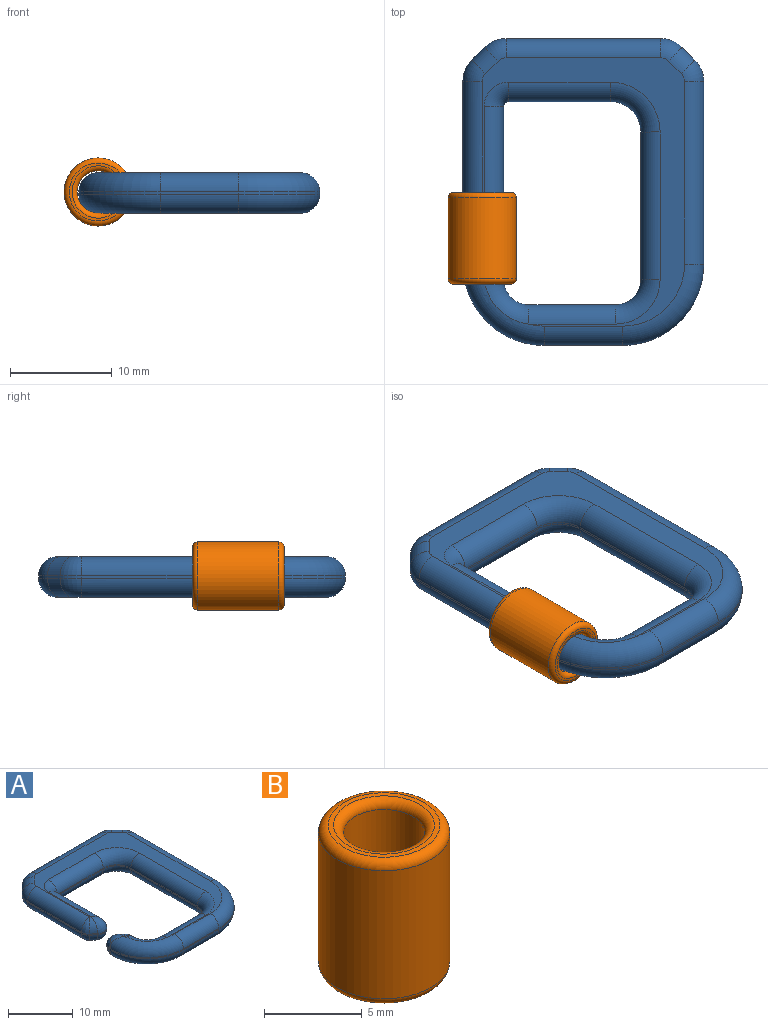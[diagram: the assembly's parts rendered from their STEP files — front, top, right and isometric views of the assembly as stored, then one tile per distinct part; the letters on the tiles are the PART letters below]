
ASSEMBLY  parts=2 mates=1
PART A: 90 faces, bbox 25x30.9x4.6 mm
  f0: plane 0.54x0.12mm, normal (0,0,-1), area 0mm2, adj f63,f66,f67,f70,f74
  f1: plane 0.54x0.12mm, normal (0,0,1), area 0mm2, adj f32,f36,f37,f42,f44
  f2: plane 15.21x0.2mm, normal (0,1,0), area 3mm2, adj f28,f31,f58,f88
  f3: plane 1.24x1.24mm, normal (-0.71,0.71,0), area 0.4mm2, adj f28,f29,f59,f87
  f4: plane 11.76x0.2mm, normal (-1,0,0), area 2.4mm2, adj f5,f29,f55,f83
  f5: cylinder r=1.5mm len=1.15mm, axis (0,0,-1), area 0.3mm2, adj f4,f6,f53,f81
  f6: plane 1x0.84mm, normal (-0.65,-0.76,0), area 0.3mm2, adj f5,f7,f51,f79
  f7: cylinder r=1.5mm len=2.47mm, axis (0,0,-1), area 0.7mm2, adj f6,f8,f49,f77
  f8: plane 10.14x0.2mm, normal (1,0,0), area 2mm2, adj f7,f9,f47,f75
  f9: cylinder r=0.5mm len=0.5mm, axis (0,0,-1), area 0.2mm2, adj f8,f10,f45,f73
  f10: plane 10x0.2mm, normal (0,-1,0), area 2mm2, adj f9,f11,f43,f69
  f11: cylinder r=3mm len=3mm, axis (0,0,-1), area 0.9mm2, adj f10,f12,f39,f64
  f12: plane 14.5x0.2mm, normal (-1,0,0), area 2.9mm2, adj f11,f13,f34,f61
  f13: cylinder r=2.5mm len=2.5mm, axis (0,0,-1), area 0.8mm2, adj f12,f14,f33,f62
  f14: plane 8.5x0.2mm, normal (0,1,0), area 1.7mm2, adj f13,f15,f38,f65
  f15: cylinder r=2.5mm len=2.5mm, axis (0,0,-1), area 0.8mm2, adj f14,f16,f42,f70
  f16: plane 0.34x0.2mm, normal (1,0,0), area 0.1mm2, adj f15,f17,f37,f66
  f17: cylinder r=2mm len=1.53mm, axis (0,0,-1), area 0.3mm2, adj f16,f18,f32,f63
  f18: plane 0.99x0.83mm, normal (0.65,0.76,0), area 0.3mm2, adj f17,f19,f36,f67
  f19: cylinder r=1.4mm len=2.3mm, axis (0,0,-1), area 0.6mm2, adj f18,f20,f35,f68
  f20: plane 0.2x0.13mm, normal (-1,0,0), area 0mm2, adj f19,f21,f40,f72
  f21: cylinder r=8mm len=8mm, axis (0,0,-1), area 2.5mm2, adj f20,f22,f44,f74
  f22: plane 7.7x0.2mm, normal (0,-1,0), area 1.5mm2, adj f21,f23,f46,f76
  f23: cylinder r=8mm len=8mm, axis (0,0,-1), area 2.5mm2, adj f22,f24,f48,f78
  f24: plane 17.96x0.2mm, normal (1,0,0), area 3.6mm2, adj f23,f30,f50,f80
  f25: plane 1.24x1.24mm, normal (0.71,0.71,0), area 0.4mm2, adj f30,f31,f54,f84
  f26: plane 26.4x19.9mm, normal (0,0,1), area 109.1mm2, adj f33,f34,f38,f39,f42,f43,f44,f45
  f27: plane 26.4x19.9mm, normal (0,0,-1), area 109.1mm2, adj f61,f62,f64,f65,f69,f70,f73,f74
  f28: cylinder r=3mm len=2.12mm, axis (0,0,-1), area 0.5mm2, adj f2,f3,f60,f89
  f29: cylinder r=3mm len=2.12mm, axis (0,0,1), area 0.5mm2, adj f3,f4,f57,f85
  f30: cylinder r=3mm len=2.12mm, axis (0,0,-1), area 0.5mm2, adj f24,f25,f52,f82
  f31: cylinder r=3mm len=2.12mm, axis (0,0,-1), area 0.5mm2, adj f2,f25,f56,f86
  f32: torus R=0.1mm, axis (0,0,1), area 3.4mm2, adj f1,f17,f36,f37
  f33: torus R=4.4mm, axis (0,0,1), area 15mm2, adj f13,f26,f34,f38
  f34: cylinder r=1.9mm len=14.5mm, axis (0,1,0), area 43.3mm2, adj f12,f26,f33,f39
  f35: bspline ~3.22x2.38mm, area 4mm2, adj f19,f36,f40,f41
  f36: cylinder r=1.9mm len=2.29mm, axis (0.76,-0.65,0), area 2.6mm2, adj f1,f18,f32,f35,f41
  f37: cylinder r=1.9mm len=1.9mm, axis (0,-1,0), area 1mm2, adj f1,f16,f32,f42
  f38: cylinder r=1.9mm len=8.5mm, axis (1,0,0), area 25.4mm2, adj f14,f26,f33,f42
  f39: torus R=4.9mm, axis (0,0,1), area 17.3mm2, adj f11,f26,f34,f43
  f40: cylinder r=1.9mm len=0.92mm, axis (0,1,0), area 0.1mm2, adj f20,f35,f44
  f41: bspline ~2.71x2.13mm, area 2mm2, adj f35,f36,f44
  f42: torus R=4.4mm, axis (0,0,1), area 14mm2, adj f1,f15,f26,f37,f38,f44
  f43: cylinder r=1.9mm len=10mm, axis (-1,0,0), area 29.8mm2, adj f10,f26,f39,f45
  f44: torus R=6.1mm, axis (0,0,1), area 32.2mm2, adj f1,f21,f26,f40,f41,f42,f46
  f45: torus R=2.4mm, axis (0,0,1), area 5.6mm2, adj f9,f26,f43,f47
  f46: cylinder r=1.9mm len=7.7mm, axis (-1,0,0), area 23mm2, adj f22,f26,f44,f48
  f47: cylinder r=1.9mm len=10.14mm, axis (0,-1,0), area 29mm2, adj f8,f26,f45,f49
  f48: torus R=6.1mm, axis (0,0,1), area 34.3mm2, adj f23,f26,f46,f50
  f49: bspline ~4.09x3.28mm, area 7mm2, adj f7,f47,f51
  f50: cylinder r=1.9mm len=17.96mm, axis (0,-1,0), area 53.6mm2, adj f24,f26,f48,f52
  f51: cylinder r=1.9mm len=2.3mm, axis (-0.76,0.65,0), area 2.7mm2, adj f6,f26,f49,f53
  f52: torus R=1.1mm, axis (0,0,1), area 5.4mm2, adj f26,f30,f50,f54
  f53: bspline ~2.19x1.9mm, area 2.5mm2, adj f5,f51,f55
  f54: cylinder r=1.9mm len=2.59mm, axis (0.71,-0.71,0), area 5.2mm2, adj f25,f26,f52,f56
  f55: cylinder r=1.9mm len=11.76mm, axis (0,1,0), area 34.8mm2, adj f4,f26,f53,f57
  f56: torus R=1.1mm, axis (0,0,1), area 5.4mm2, adj f26,f31,f54,f58
  f57: torus R=1.1mm, axis (0,0,1), area 5.4mm2, adj f26,f29,f55,f59
  f58: cylinder r=1.9mm len=15.21mm, axis (1,0,0), area 45.4mm2, adj f2,f26,f56,f60
  f59: cylinder r=1.9mm len=2.59mm, axis (0.71,0.71,0), area 5.2mm2, adj f3,f26,f57,f60
  f60: torus R=1.1mm, axis (0,0,1), area 5.4mm2, adj f26,f28,f58,f59
  f61: cylinder r=1.9mm len=14.5mm, axis (0,-1,0), area 43.3mm2, adj f12,f27,f62,f64
  f62: torus R=4.4mm, axis (0,0,1), area 15mm2, adj f13,f27,f61,f65
  f63: torus R=0.1mm, axis (0,0,1), area 3.4mm2, adj f0,f17,f66,f67
  f64: torus R=4.9mm, axis (0,0,1), area 17.3mm2, adj f11,f27,f61,f69
  f65: cylinder r=1.9mm len=8.5mm, axis (-1,0,0), area 25.4mm2, adj f14,f27,f62,f70
  f66: cylinder r=1.9mm len=1.9mm, axis (0,1,0), area 1mm2, adj f0,f16,f63,f70
  f67: cylinder r=1.9mm len=2.29mm, axis (-0.76,0.65,0), area 2.6mm2, adj f0,f18,f63,f68,f71
  f68: bspline ~3.22x2.38mm, area 4mm2, adj f19,f67,f71,f72
  f69: cylinder r=1.9mm len=10mm, axis (1,0,0), area 29.8mm2, adj f10,f27,f64,f73
  f70: torus R=4.4mm, axis (0,0,1), area 14mm2, adj f0,f15,f27,f65,f66,f74
  f71: bspline ~2.71x2.13mm, area 2mm2, adj f67,f68,f74
  f72: cylinder r=1.9mm len=0.92mm, axis (0,-1,0), area 0.1mm2, adj f20,f68,f74
  f73: torus R=2.4mm, axis (0,0,1), area 5.6mm2, adj f9,f27,f69,f75
  f74: torus R=6.1mm, axis (0,0,1), area 32.2mm2, adj f0,f21,f27,f70,f71,f72,f76
  f75: cylinder r=1.9mm len=10.14mm, axis (0,1,0), area 29mm2, adj f8,f27,f73,f77
  f76: cylinder r=1.9mm len=7.7mm, axis (1,0,0), area 23mm2, adj f22,f27,f74,f78
  f77: bspline ~4.09x3.28mm, area 7mm2, adj f7,f75,f79
  f78: torus R=6.1mm, axis (0,0,1), area 34.3mm2, adj f23,f27,f76,f80
  f79: cylinder r=1.9mm len=2.3mm, axis (0.76,-0.65,0), area 2.7mm2, adj f6,f27,f77,f81
  f80: cylinder r=1.9mm len=17.96mm, axis (0,1,0), area 53.6mm2, adj f24,f27,f78,f82
  f81: bspline ~2.19x1.9mm, area 2.5mm2, adj f5,f79,f83
  f82: torus R=1.1mm, axis (0,0,1), area 5.4mm2, adj f27,f30,f80,f84
  f83: cylinder r=1.9mm len=11.76mm, axis (0,-1,0), area 34.8mm2, adj f4,f27,f81,f85
  f84: cylinder r=1.9mm len=2.59mm, axis (-0.71,0.71,0), area 5.2mm2, adj f25,f27,f82,f86
  f85: torus R=1.1mm, axis (0,0,1), area 5.4mm2, adj f27,f29,f83,f87
  f86: torus R=1.1mm, axis (0,0,1), area 5.4mm2, adj f27,f31,f84,f88
  f87: cylinder r=1.9mm len=2.59mm, axis (-0.71,-0.71,0), area 5.2mm2, adj f3,f27,f85,f89
  f88: cylinder r=1.9mm len=15.21mm, axis (-1,0,0), area 45.4mm2, adj f2,f27,f86,f89
  f89: torus R=1.1mm, axis (0,0,1), area 5.4mm2, adj f27,f28,f87,f88
PART B: 8 faces, bbox 7.3x7.3x9 mm
  f0: cylinder r=2.08mm len=8mm, axis (0,0,-1), area 104.3mm2, adj f4,f6
  f1: cylinder r=3.35mm len=8mm, axis (0,0,-1), area 168.4mm2, adj f5,f7
  f2: plane 5.7x5.7mm, normal (0,0,1), area 4.7mm2, adj f6,f7
  f3: plane 5.7x5.7mm, normal (0,0,-1), area 4.7mm2, adj f4,f5
  f4: torus R=2.58mm, axis (0,0,1), area 11.1mm2, adj f0,f3
  f5: torus R=2.85mm, axis (0,0,1), area 15.6mm2, adj f1,f3
  f6: torus R=2.58mm, axis (0,0,1), area 11.1mm2, adj f0,f2
  f7: torus R=2.85mm, axis (0,0,1), area 15.6mm2, adj f1,f2
PLACE A t=(-2.64,0.19,-0.93)mm fixed
PLACE B rot(axis=(-0.47,-0.62,-0.62),129.6deg) t=(-11.49,-7.76,1.17)mm
MATE cylindrical B.f0 <-> A.f40  axis (0,-1,0) through (-11.49,0.74,1.17)mm
